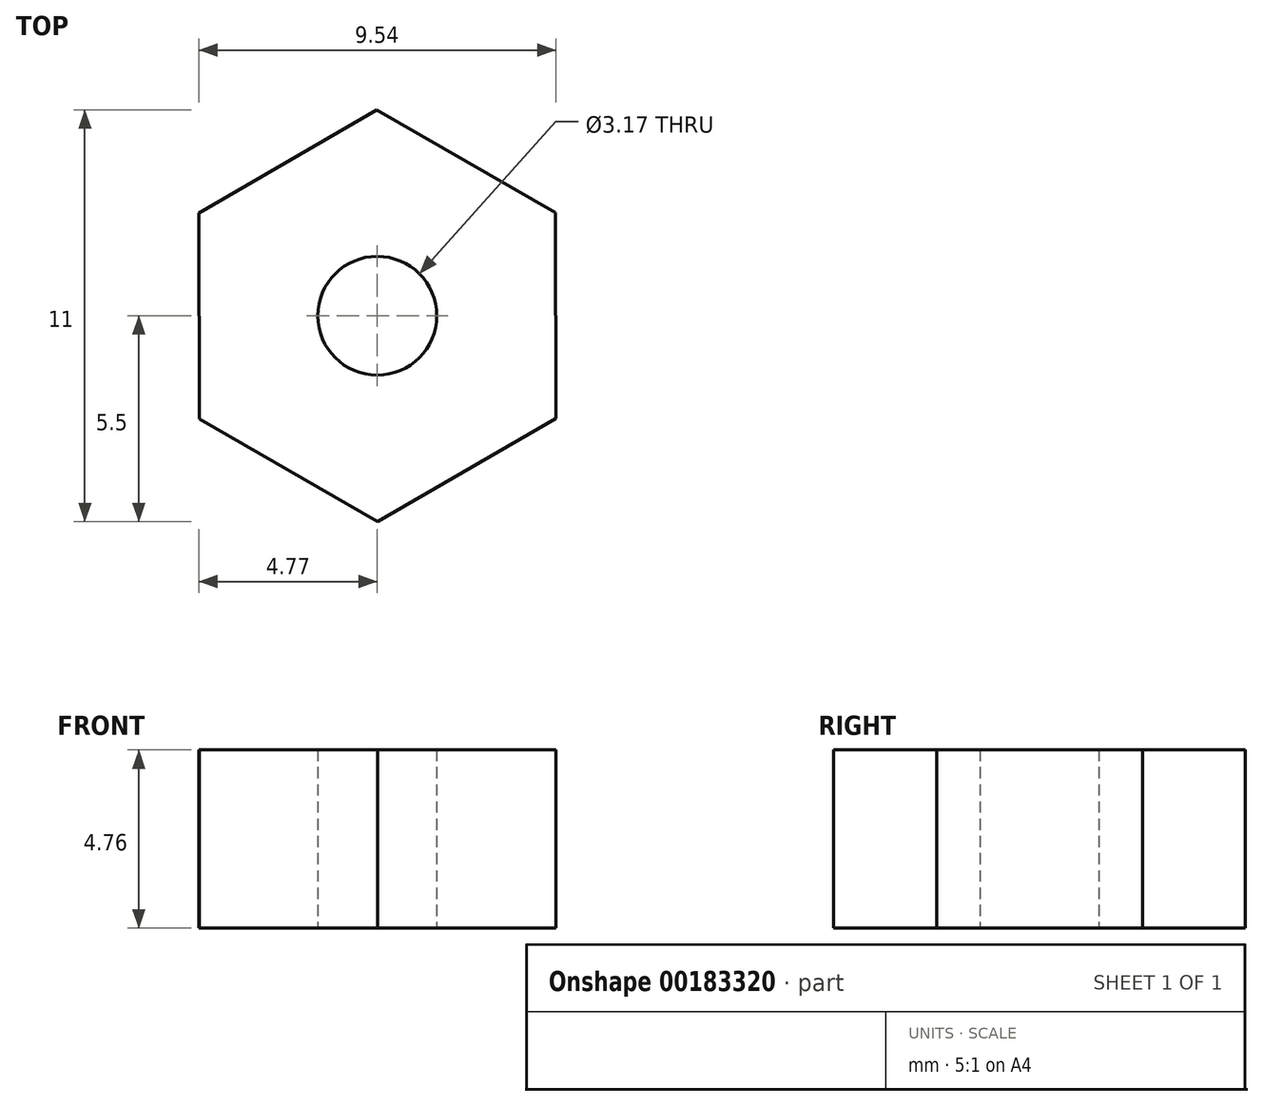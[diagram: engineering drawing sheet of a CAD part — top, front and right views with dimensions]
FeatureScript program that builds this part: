
annotation { "Feature Type Name" : "Feature", "Feature Type Description" : "" }
export const myFeature = defineFeature(function(context is Context, id is Id, definition is map)
    precondition{}
    {
        {
            var Q0;
            Q0=qCreatedBy(makeId("Top.planeOp"),FACE);
            var sketch = newSketch(context, id + "F0", { "sketchPlane" : qUnion([Q0])});
            skCircle(sketch, "E0.cCircle", {"center": v(0, 0) * mm, "radius": 4.76 * mm, "construction": true});
            skLineSegment(sketch, "E0.0", {"start": v(0, -5.5) * mm, "end": v(-4.76, -2.76) * mm});
            skLineSegment(sketch, "E0.1", {"start": v(-4.76, -2.76) * mm, "end": v(-4.77, 2.74) * mm});
            skLineSegment(sketch, "E0.2", {"start": v(-4.77, 2.74) * mm, "end": v(0, 5.5) * mm});
            skLineSegment(sketch, "E0.3", {"start": v(0, 5.5) * mm, "end": v(4.76, 2.76) * mm});
            skLineSegment(sketch, "E0.4", {"start": v(4.76, 2.76) * mm, "end": v(4.77, -2.74) * mm});
            skLineSegment(sketch, "E0.5", {"start": v(4.77, -2.74) * mm, "end": v(0, -5.5) * mm});
            skPoint(sketch, "E0.0.midPoint", {"position": v(-2.37, -4.13) * mm});
            skCircle(sketch, "E1", {"center": v(0, 0) * mm, "radius": 1.59 * mm});
            skSolve(sketch);
        }
        {
            var Q0;
            Q0 = qSketchRegion(id + "F0", true);
            extrude(context, id + "F1", {"entities" : qUnion([Q0]), "depth" : 4.76 * mm});
        }
    });
